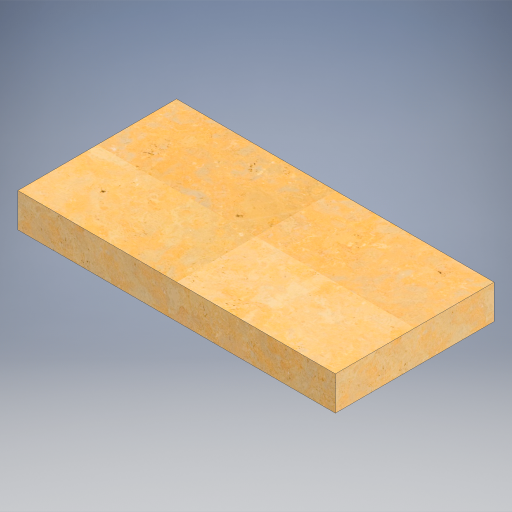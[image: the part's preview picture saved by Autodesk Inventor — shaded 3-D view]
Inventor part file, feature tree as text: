
AUTODESK INVENTOR PART (.ipt)
format: ipt  version: 2023 (Build 270158030, 158C)  size: 424,960 bytes
history: native  units: in
note: dims shown in document units (in); Inventor stores cm internally (conversion verified against a paired STEP export)
features: extrude x1, sketch x1
ambient origin geometry x8: Origin, YZ Plane, XZ Plane, XY Plane, X Axis, Y Axis, Z Axis, Center Point
bodies: Solid1 (feature_tree)
feature tree (2):
  extrude  "Extrusion1"  Depth=14.0in
  sketch  "Sketch1"  dims[d0=28.0in d1=14.0in d2=3.0in d3=0.0in]
